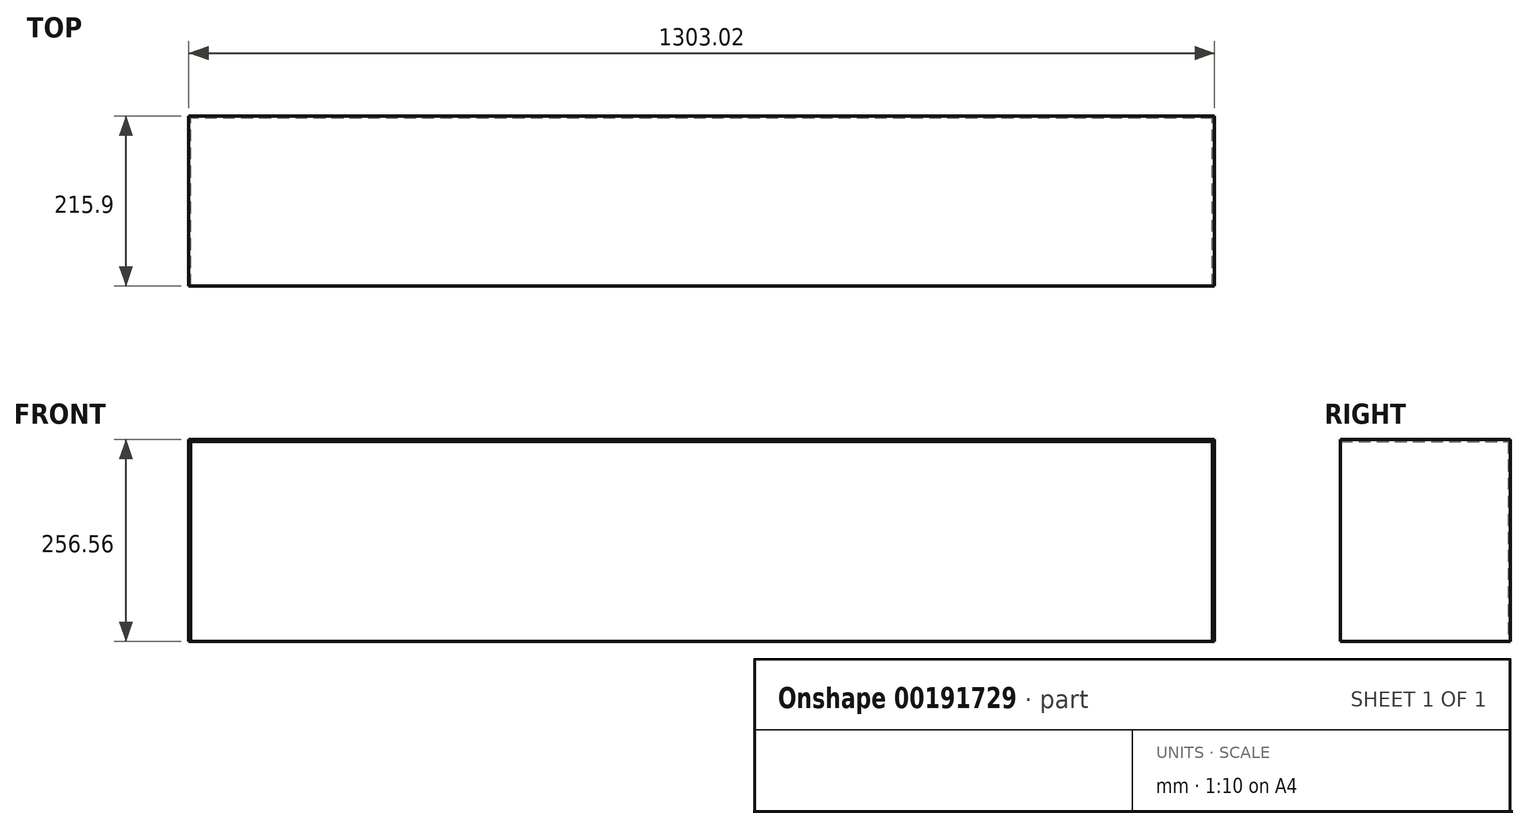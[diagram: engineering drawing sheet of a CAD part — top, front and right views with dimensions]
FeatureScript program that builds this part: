
annotation { "Feature Type Name" : "Feature", "Feature Type Description" : "" }
export const myFeature = defineFeature(function(context is Context, id is Id, definition is map)
    precondition{}
    {
        {
            var Q0;
            Q0=qCreatedBy(makeId("Front.planeOp"),FACE);
            var sketch = newSketch(context, id + "F0", { "sketchPlane" : qUnion([Q0])});
            skLineSegment(sketch, "E0.bottom", {"start": v(-67.83, 129.99) * mm, "end": v(1235.2, 129.99) * mm});
            skLineSegment(sketch, "E0.left", {"start": v(-67.83, 129.99) * mm, "end": v(-67.83, -24.95) * mm});
            skLineSegment(sketch, "E0.right", {"start": v(1235.2, 129.99) * mm, "end": v(1235.2, -24.95) * mm});
            skLineSegment(sketch, "E1.bottom", {"start": v(-65.29, 127.45) * mm, "end": v(1232.65, 127.45) * mm});
            skLineSegment(sketch, "E1.left", {"start": v(-65.29, 127.45) * mm, "end": v(-65.29, -24.95) * mm});
            skLineSegment(sketch, "E1.right", {"start": v(1232.65, 127.45) * mm, "end": v(1232.65, 25.85) * mm});
            skLineSegment(sketch, "E2", {"start": v(1232.65, 25.85) * mm, "end": v(1232.65, -126.55) * mm});
            skLineSegment(sketch, "E3", {"start": v(1235.2, -24.95) * mm, "end": v(1235.2, -126.55) * mm});
            skLineSegment(sketch, "E4", {"start": v(1232.65, -126.55) * mm, "end": v(-60.99, -126.55) * mm});
            skLineSegment(sketch, "E5", {"start": v(-60.99, -126.55) * mm, "end": v(-65.29, -126.55) * mm});
            skLineSegment(sketch, "E6", {"start": v(-65.29, -24.95) * mm, "end": v(-65.29, -126.55) * mm});
            skLineSegment(sketch, "E7", {"start": v(-67.83, -24.95) * mm, "end": v(-67.83, -126.57) * mm});
            skLineSegment(sketch, "E8", {"start": v(-67.83, -126.57) * mm, "end": v(-65.29, -126.55) * mm});
            skLineSegment(sketch, "E9", {"start": v(1235.2, -126.55) * mm, "end": v(1232.65, -126.55) * mm});
            skSolve(sketch);
        }
        {
            var Q0;
            Q0=makeQuery(id+"F0.imprint","IMPRINT",FACE,{"disambiguationData":[TD([[makeQuery(id+"F0.imprint","IMPRINT",EDGE,{"derivedFrom":sQuery(id+"F0.wireOp",EDGE,"E1.bottom")}),-1.0]])]});
            extrude(context, id + "F1", {"entities" : qUnion([Q0]), "depth" : 2.54 * mm});
        }
        {
            var Q0;
            Q0=makeQuery(id+"F0.imprint","IMPRINT",FACE,{"disambiguationData":[TD([[makeQuery(id+"F0.imprint","IMPRINT",EDGE,{"derivedFrom":sQuery(id+"F0.wireOp",EDGE,"E0.bottom")}),-1.0]])]});
            extrude(context, id + "F2", {"entities" : qUnion([Q0]), "operationType" : NewBodyOperationType.ADD, "depth" : 215.9 * mm});
        }
    });
